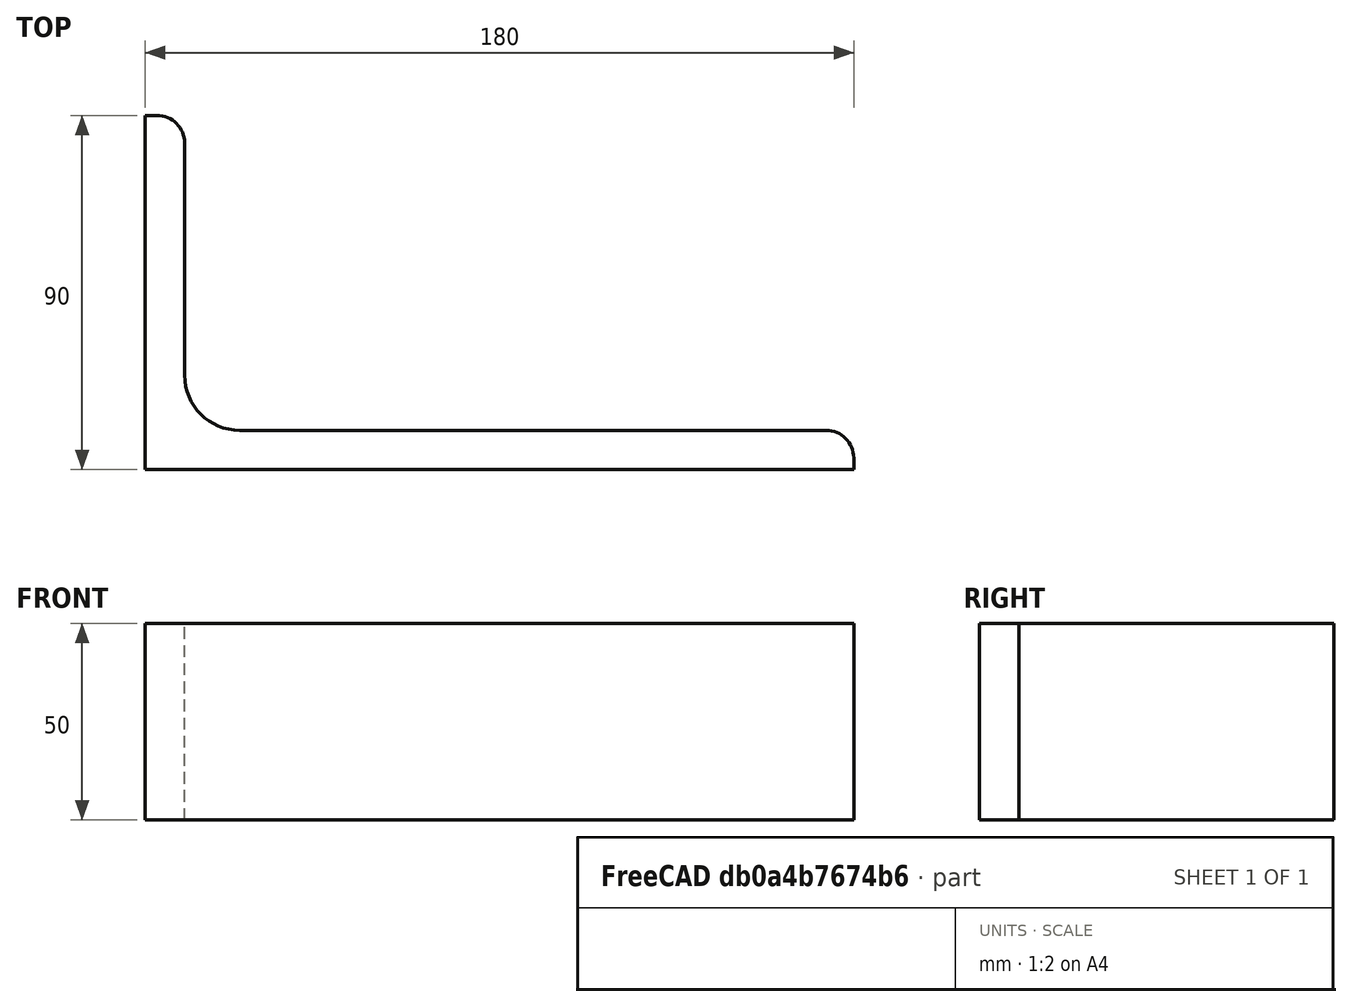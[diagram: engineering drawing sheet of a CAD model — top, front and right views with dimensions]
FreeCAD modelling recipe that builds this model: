
FCSTD DOCUMENT  (FreeCAD 0.15R4671 (Git))
Label: Angle Bar 180x90x10 EN10056 S235JR
License: All rights reserved
LicenseURL: http://en.wikipedia.org/wiki/All_rights_reserved
objects: Sketcher::SketchObject×1, Part::Extrusion×1
note: 2 computed .brp shape members not serialized (recipe doc carries the construction recipe); baked Part::Feature solids carry a one-line shape summary decoded from their .brp

FEATURE [Sketcher::SketchObject] Sketch
  sketch-geometry (9):
    g0: LineSegment StartX=0 StartY=0 StartZ=0 EndX=180 EndY=0 EndZ=0
    g1: LineSegment StartX=180 StartY=0 StartZ=0 EndX=180 EndY=3 EndZ=0
    g2: LineSegment StartX=173 StartY=10 StartZ=0 EndX=24 EndY=10 EndZ=0
    g3: LineSegment StartX=0 StartY=0 StartZ=0 EndX=0 EndY=90 EndZ=0
    g4: LineSegment StartX=0 StartY=90 StartZ=0 EndX=3 EndY=90 EndZ=0
    g5: LineSegment StartX=10 StartY=83 StartZ=0 EndX=10 EndY=24 EndZ=0
    g6: ArcOfCircle CenterX=24 CenterY=24 CenterZ=0 NormalX=0 NormalY=0 NormalZ=1 Radius=14 StartAngle=3.14159 EndAngle=4.71239
    g7: ArcOfCircle CenterX=3 CenterY=83 CenterZ=0 NormalX=0 NormalY=0 NormalZ=1 Radius=7 StartAngle=0 EndAngle=1.5708
    g8: ArcOfCircle CenterX=173 CenterY=3 CenterZ=0 NormalX=0 NormalY=0 NormalZ=1 Radius=7 StartAngle=0 EndAngle=1.5708
  constraints (23):
    c: Coincident(g0,g-1)
    c: Horizontal(g0)
    c: Coincident(g1,g0)
    c: Vertical(g1)
    c: Horizontal(g2)
    c: Coincident(g3,g-1)
    c: Vertical(g3)
    c: Coincident(g4,g3)
    c: Horizontal(g4)
    c: Vertical(g5)
    c: Tangent(g5,g6) = -1.5708
    c: Tangent(g2,g6) = 1.5708
    c: Tangent(g4,g7) = 1.5708
    c: Tangent(g5,g7) = 1.5708
    c: Tangent(g2,g8) = -1.5708
    c: Tangent(g1,g8) = -1.5708
    c: DistanceX(g0) = 180
    c: DistanceY(g3) = 90
    c: DistanceY(g0,g2) = 10
    c: DistanceX(g3,g5) = 10
    c: Radius(g6) = 14
    c: Radius(g8) = 7
    c: Radius(g7) = 7
FEATURE [Part::Extrusion] Extrude  label="Angle Bar 180x90x10 EN10056 S235JR"
  Base = -> Sketch
  Dir = (0,0,50)
  Solid = true
